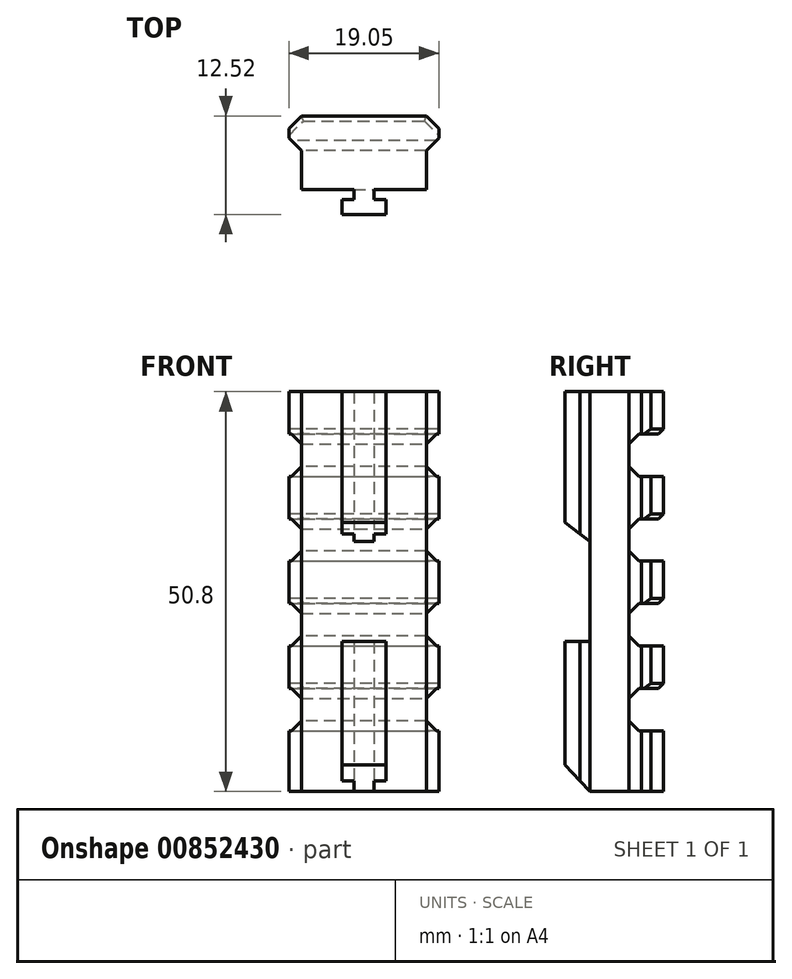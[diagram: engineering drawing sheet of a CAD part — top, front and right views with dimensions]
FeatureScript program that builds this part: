
annotation { "Feature Type Name" : "Feature", "Feature Type Description" : "" }
export const myFeature = defineFeature(function(context is Context, id is Id, definition is map)
    precondition{}
    {
        {
            var Q0;
            Q0=qCreatedBy(makeId("Top.planeOp"),FACE);
            var sketch = newSketch(context, id + "F0", { "sketchPlane" : qUnion([Q0])});
            skLineSegment(sketch, "E0.bottom", {"start": v(5.5, 6.04) * mm, "end": v(21.38, 6.04) * mm});
            skLineSegment(sketch, "E0.top", {"start": v(5.5, 11) * mm, "end": v(21.38, 11) * mm});
            skLineSegment(sketch, "E0.left", {"start": v(5.5, 6.04) * mm, "end": v(5.5, 11) * mm});
            skLineSegment(sketch, "E0.right", {"start": v(21.38, 6.04) * mm, "end": v(21.38, 11) * mm});
            skSolve(sketch);
        }
        {
            var Q0;
            Q0 = qSketchRegion(id + "F0", true);
            extrude(context, id + "F1", {"entities" : qUnion([Q0]), "depth" : 50.8 * mm, "offsetDistance" : 25.4 * mm});
        }
        {
            var Q0;
            Q0=makeQuery(id+"F1.opExtrude","CAP_FACE",FACE,{"disambiguationData":[OSD([sQuery(id+"F0.wireOp",EDGE,"E0.bottom"),sQuery(id+"F0.wireOp",EDGE,"E0.top"),sQuery(id+"F0.wireOp",EDGE,"E0.left"),sQuery(id+"F0.wireOp",EDGE,"E0.right")])],"isStart":false});
            var sketch = newSketch(context, id + "F2", { "sketchPlane" : qUnion([Q0])});
            skLineSegment(sketch, "E1", {"start": v(5.5, 11) * mm, "end": v(3.92, 12.58) * mm});
            skLineSegment(sketch, "E2", {"start": v(3.92, 12.58) * mm, "end": v(3.92, 13.8) * mm});
            skLineSegment(sketch, "E3", {"start": v(3.92, 13.8) * mm, "end": v(5.5, 15.39) * mm});
            skLineSegment(sketch, "E4", {"start": v(13.44, 12.67) * mm, "end": v(13.44, 17.63) * mm, "construction": true});
            skPoint(sketch, "E4.startSnap0", {"position": v(13.44, 11) * mm});
            skLineSegment(sketch, "E5.MirrorCS", {"start": v(22.97, 13.8) * mm, "end": v(21.38, 15.39) * mm});
            skLineSegment(sketch, "E6.MirrorCS", {"start": v(22.97, 12.58) * mm, "end": v(22.97, 13.8) * mm});
            skLineSegment(sketch, "E7.MirrorCS", {"start": v(21.38, 11) * mm, "end": v(22.97, 12.58) * mm});
            skLineSegment(sketch, "E8", {"start": v(5.5, 15.39) * mm, "end": v(21.38, 15.39) * mm});
            skSolve(sketch);
        }
        {
            var Q0;
            Q0 = qSketchRegion(id + "F2", true);
            var Q1;
            Q1=makeQuery(id+"F2.imprint","IMPRINT",FACE,{"disambiguationData":[TD([[makeQuery(id+"F2.imprint","IMPRINT",EDGE,{"derivedFrom":sQuery(id+"F2.wireOp",EDGE,"E1")}),-1.0]])]});
            extrude(context, id + "F3", {"entities" : qUnion([Q0, Q1]), "operationType" : NewBodyOperationType.ADD, "oppositeDirection" : true, "depth" : 50.8 * mm, "offsetDistance" : 25.4 * mm});
        }
        {
            var Q0;
            {var subQ0=sQuery(id+"F0.wireOp",EDGE,"E0.top");Q0=makeQuery(id+"F3.boolean.opBoolean","MERGE",FACE,{"derivedFrom":[makeQuery(id+"F1.opExtrude","CAP_FACE",FACE,{"disambiguationData":[OSD([sQuery(id+"F0.wireOp",EDGE,"E0.bottom"),subQ0,sQuery(id+"F0.wireOp",EDGE,"E0.left"),sQuery(id+"F0.wireOp",EDGE,"E0.right")])],"isStart":false}),makeQuery(id+"F3.opExtrude","CAP_FACE",FACE,{"disambiguationData":[OSD([subQ0,sQuery(id+"F2.wireOp",EDGE,"E1"),sQuery(id+"F2.wireOp",EDGE,"E2"),sQuery(id+"F2.wireOp",EDGE,"E3"),sQuery(id+"F2.wireOp",EDGE,"E5.MirrorCS"),sQuery(id+"F2.wireOp",EDGE,"E6.MirrorCS"),sQuery(id+"F2.wireOp",EDGE,"E7.MirrorCS"),sQuery(id+"F2.wireOp",EDGE,"E8")])],"isStart":true})]});}
            var sketch = newSketch(context, id + "F4", { "sketchPlane" : qUnion([Q0])});
            skLineSegment(sketch, "E9.bottom", {"start": v(16.24, 6.04) * mm, "end": v(10.65, 6.04) * mm});
            skLineSegment(sketch, "E9.top", {"start": v(16.24, 2.87) * mm, "end": v(10.65, 2.87) * mm});
            skLineSegment(sketch, "E9.left", {"start": v(16.24, 6.04) * mm, "end": v(16.24, 2.87) * mm});
            skLineSegment(sketch, "E9.right", {"start": v(10.65, 6.04) * mm, "end": v(10.65, 2.87) * mm});
            skSolve(sketch);
        }
        {
            var Q0;
            Q0 = qSketchRegion(id + "F4", true);
            var Q1;
            {var subQ0=sQuery(id+"F0.wireOp",EDGE,"E0.top");Q1=makeQuery(id+"F3.boolean.opBoolean","MERGE",FACE,{"derivedFrom":[makeQuery(id+"F1.opExtrude","CAP_FACE",FACE,{"disambiguationData":[OSD([sQuery(id+"F0.wireOp",EDGE,"E0.bottom"),subQ0,sQuery(id+"F0.wireOp",EDGE,"E0.left"),sQuery(id+"F0.wireOp",EDGE,"E0.right")])],"isStart":true}),makeQuery(id+"F3.opExtrude","CAP_FACE",FACE,{"disambiguationData":[OSD([subQ0,sQuery(id+"F2.wireOp",EDGE,"E1"),sQuery(id+"F2.wireOp",EDGE,"E2"),sQuery(id+"F2.wireOp",EDGE,"E3"),sQuery(id+"F2.wireOp",EDGE,"E5.MirrorCS"),sQuery(id+"F2.wireOp",EDGE,"E6.MirrorCS"),sQuery(id+"F2.wireOp",EDGE,"E7.MirrorCS"),sQuery(id+"F2.wireOp",EDGE,"E8")])],"isStart":false})]});}
            extrude(context, id + "F5", {"entities" : qUnion([Q0]), "operationType" : NewBodyOperationType.ADD, "endBound" : BoundingType.UP_TO_SURFACE, "oppositeDirection" : true, "depth" : 25.4 * mm, "endBoundEntityFace" : qUnion([Q1]), "offsetDistance" : 25.4 * mm});
        }
        {
            var Q0;
            Q0=makeQuery(id+"F5.opExtrude","SWEPT_FACE",FACE,{"disambiguationData":[OSD([sQuery(id+"F4.wireOp",EDGE,"E9.top")])]});
            var sketch = newSketch(context, id + "F6", { "sketchPlane" : qUnion([Q0])});
            skLineSegment(sketch, "E10.bottom", {"start": v(16.24, 19.05) * mm, "end": v(10.65, 19.05) * mm});
            skLineSegment(sketch, "E10.top", {"start": v(16.24, 31.75) * mm, "end": v(10.65, 31.75) * mm});
            skLineSegment(sketch, "E10.left", {"start": v(16.24, 19.05) * mm, "end": v(16.24, 31.75) * mm});
            skLineSegment(sketch, "E10.right", {"start": v(10.65, 19.05) * mm, "end": v(10.65, 31.75) * mm});
            skSolve(sketch);
        }
        {
            var Q0;
            Q0 = qSketchRegion(id + "F6", true);
            var Q1;
            {var subQ9=sQuery(id+"F0.wireOp",EDGE,"E0.left");var subQ10=sQuery(id+"F0.wireOp",EDGE,"E0.bottom");Q1=makeQuery(id+"F5.boolean.opBoolean","SPLIT",FACE,{"disambiguationData":[TD([makeQuery(id+"F1.opExtrude","SWEPT_FACE",FACE,{"disambiguationData":[OSD([subQ9])]})])],"derivedFrom":makeQuery(id+"F1.opExtrude","SWEPT_FACE",FACE,{"disambiguationData":[OSD([subQ10])]})});}
            extrude(context, id + "F7", {"entities" : qUnion([Q0]), "operationType" : NewBodyOperationType.REMOVE, "endBound" : BoundingType.UP_TO_SURFACE, "oppositeDirection" : true, "depth" : 25.4 * mm, "endBoundEntityFace" : qUnion([Q1]), "offsetDistance" : 25.4 * mm});
        }
        {
            var Q0;
            {var subQ0=sQuery(id+"F0.wireOp",EDGE,"E0.top");Q0=makeQuery(id+"F5.boolean.opBoolean","MERGE",FACE,{"derivedFrom":[makeQuery(id+"F3.boolean.opBoolean","MERGE",FACE,{"derivedFrom":[makeQuery(id+"F1.opExtrude","CAP_FACE",FACE,{"disambiguationData":[OSD([sQuery(id+"F0.wireOp",EDGE,"E0.bottom"),subQ0,sQuery(id+"F0.wireOp",EDGE,"E0.left"),sQuery(id+"F0.wireOp",EDGE,"E0.right")])],"isStart":true}),makeQuery(id+"F3.opExtrude","CAP_FACE",FACE,{"disambiguationData":[OSD([subQ0,sQuery(id+"F2.wireOp",EDGE,"E1"),sQuery(id+"F2.wireOp",EDGE,"E2"),sQuery(id+"F2.wireOp",EDGE,"E3"),sQuery(id+"F2.wireOp",EDGE,"E5.MirrorCS"),sQuery(id+"F2.wireOp",EDGE,"E6.MirrorCS"),sQuery(id+"F2.wireOp",EDGE,"E7.MirrorCS"),sQuery(id+"F2.wireOp",EDGE,"E8")])],"isStart":false})]}),makeQuery(id+"F5.opExtrude","CAP_FACE",FACE,{"disambiguationData":[OSD([sQuery(id+"F4.wireOp",EDGE,"E9.bottom"),sQuery(id+"F4.wireOp",EDGE,"E9.top"),sQuery(id+"F4.wireOp",EDGE,"E9.left"),sQuery(id+"F4.wireOp",EDGE,"E9.right")])],"isStart":false})]});}
            var sketch = newSketch(context, id + "F8", { "sketchPlane" : qUnion([Q0])});
            skLineSegment(sketch, "E11.bottom", {"start": v(16.24, -6.04) * mm, "end": v(14.71, -6.04) * mm});
            skLineSegment(sketch, "E11.top", {"start": v(16.24, -4.77) * mm, "end": v(14.71, -4.77) * mm});
            skLineSegment(sketch, "E11.left", {"start": v(16.24, -6.04) * mm, "end": v(16.24, -4.77) * mm});
            skLineSegment(sketch, "E11.right", {"start": v(14.71, -6.04) * mm, "end": v(14.71, -4.77) * mm});
            skLineSegment(sketch, "E12", {"start": v(13.44, -2.87) * mm, "end": v(13.44, -7.3) * mm, "construction": true});
            skLineSegment(sketch, "E13.MirrorCS", {"start": v(12.17, -6.04) * mm, "end": v(12.17, -4.77) * mm});
            skLineSegment(sketch, "E14.MirrorCS", {"start": v(10.65, -6.04) * mm, "end": v(12.17, -6.04) * mm});
            skLineSegment(sketch, "E15.MirrorCS", {"start": v(10.65, -4.77) * mm, "end": v(12.17, -4.77) * mm});
            skSolve(sketch);
        }
        {
            var Q0;
            Q0 = qSketchRegion(id + "F8", true);
            var Q1;
            Q1=makeQuery(id+"F8.imprint","IMPRINT",FACE,{"disambiguationData":[TD([[makeQuery(id+"F8.imprint","IMPRINT",EDGE,{"derivedFrom":sQuery(id+"F8.wireOp",EDGE,"E13.MirrorCS")}),1.0]])]});
            extrude(context, id + "F9", {"entities" : qUnion([Q0, Q1]), "operationType" : NewBodyOperationType.REMOVE, "endBound" : BoundingType.THROUGH_ALL, "oppositeDirection" : true, "depth" : 25.4 * mm, "offsetDistance" : 25.4 * mm});
        }
        {
            var Q0;
            {var subQ2=sQuery(id+"F4.wireOp",EDGE,"E9.left");var subQ4=sQuery(id+"F6.wireOp",EDGE,"E10.bottom");Q0=makeQuery(id+"F7.boolean.opBoolean","SPLIT",FACE,{"disambiguationData":[TD([makeQuery(id+"F7.opExtrude","SWEPT_FACE",FACE,{"disambiguationData":[OSD([subQ4])]})])],"derivedFrom":makeQuery(id+"F5.opExtrude","SWEPT_FACE",FACE,{"disambiguationData":[OSD([subQ2])]})});}
            var sketch = newSketch(context, id + "F10", { "sketchPlane" : qUnion([Q0])});
            skLineSegment(sketch, "E16", {"start": v(2.87, 3.4) * mm, "end": v(6.04, 0) * mm});
            skLineSegment(sketch, "E17", {"start": v(2.87, 34.2) * mm, "end": v(6.04, 31.75) * mm});
            skLineSegment(sketch, "E18", {"start": v(6.04, 0) * mm, "end": v(2.87, 0) * mm});
            skLineSegment(sketch, "E19", {"start": v(2.87, 0) * mm, "end": v(2.87, 3.4) * mm});
            skLineSegment(sketch, "E20", {"start": v(2.87, 34.2) * mm, "end": v(2.87, 31.75) * mm});
            skLineSegment(sketch, "E21", {"start": v(2.87, 31.75) * mm, "end": v(6.04, 31.75) * mm});
            skSolve(sketch);
        }
        {
            var Q0;
            Q0 = qSketchRegion(id + "F10", true);
            extrude(context, id + "F11", {"entities" : qUnion([Q0]), "operationType" : NewBodyOperationType.REMOVE, "endBound" : BoundingType.UP_TO_NEXT, "oppositeDirection" : true, "depth" : 25.4 * mm, "offsetDistance" : 25.4 * mm});
        }
        {
            var Q0;
            Q0=makeQuery(id+"F1.opExtrude","SWEPT_FACE",FACE,{"disambiguationData":[OSD([sQuery(id+"F0.wireOp",EDGE,"E0.right")])]});
            var sketch = newSketch(context, id + "F12", { "sketchPlane" : qUnion([Q0])});
            skLineSegment(sketch, "E22.bottom", {"start": v(11, 45.42) * mm, "end": v(15.39, 45.42) * mm});
            skLineSegment(sketch, "E22.top", {"start": v(11, 40.03) * mm, "end": v(15.39, 40.03) * mm});
            skLineSegment(sketch, "E22.left", {"start": v(11, 45.42) * mm, "end": v(11, 40.03) * mm});
            skLineSegment(sketch, "E22.right", {"start": v(15.39, 45.42) * mm, "end": v(15.39, 40.03) * mm});
            skLineSegment(sketch, "E23.bottom", {"start": v(11, 34.65) * mm, "end": v(15.39, 34.65) * mm});
            skLineSegment(sketch, "E23.top", {"start": v(11, 29.26) * mm, "end": v(15.39, 29.26) * mm});
            skLineSegment(sketch, "E23.left", {"start": v(11, 34.65) * mm, "end": v(11, 29.26) * mm});
            skLineSegment(sketch, "E23.right", {"start": v(15.39, 34.65) * mm, "end": v(15.39, 29.26) * mm});
            skLineSegment(sketch, "E24.bottom", {"start": v(11, 23.88) * mm, "end": v(15.39, 23.88) * mm});
            skLineSegment(sketch, "E24.top", {"start": v(11, 18.5) * mm, "end": v(15.39, 18.5) * mm});
            skLineSegment(sketch, "E24.left", {"start": v(11, 23.88) * mm, "end": v(11, 18.5) * mm});
            skLineSegment(sketch, "E24.right", {"start": v(15.39, 23.88) * mm, "end": v(15.39, 18.5) * mm});
            skLineSegment(sketch, "E25.bottom", {"start": v(11, 13.1) * mm, "end": v(15.39, 13.1) * mm});
            skLineSegment(sketch, "E25.top", {"start": v(11, 7.72) * mm, "end": v(15.39, 7.72) * mm});
            skLineSegment(sketch, "E25.left", {"start": v(11, 13.1) * mm, "end": v(11, 7.72) * mm});
            skLineSegment(sketch, "E25.right", {"start": v(15.39, 13.1) * mm, "end": v(15.39, 7.72) * mm});
            skSolve(sketch);
        }
        {
            var Q0;
            Q0 = qSketchRegion(id + "F12", true);
            extrude(context, id + "F13", {"entities" : qUnion([Q0]), "operationType" : NewBodyOperationType.REMOVE, "endBound" : BoundingType.SYMMETRIC, "oppositeDirection" : true, "depth" : 50.8 * mm, "offsetDistance" : 25.4 * mm});
        }
        {
            var Q0;
            Q0=makeQuery(id+"F13.boolean.opBoolean","COPY",EDGE,{"derivedFrom":makeQuery(id+"F13.opExtrude","SWEPT_EDGE",EDGE,{"disambiguationData":[OSD([sQuery(id+"F0.wireOp",EDGE,"E0.top"),sQuery(id+"F0.wireOp",EDGE,"E0.right"),sQuery(id+"F2.wireOp",EDGE,"E7.MirrorCS"),sQuery(id+"F12.wireOp",EDGE,"E25.top"),sQuery(id+"F12.wireOp",EDGE,"E25.left")])]})});
            var Q1;
            Q1=makeQuery(id+"F13.boolean.opBoolean","COPY",EDGE,{"derivedFrom":makeQuery(id+"F13.opExtrude","SWEPT_EDGE",EDGE,{"disambiguationData":[OSD([sQuery(id+"F0.wireOp",EDGE,"E0.top"),sQuery(id+"F0.wireOp",EDGE,"E0.right"),sQuery(id+"F2.wireOp",EDGE,"E7.MirrorCS"),sQuery(id+"F12.wireOp",EDGE,"E25.bottom"),sQuery(id+"F12.wireOp",EDGE,"E25.left")])]})});
            var Q2;
            Q2=makeQuery(id+"F13.boolean.opBoolean","COPY",EDGE,{"derivedFrom":makeQuery(id+"F13.opExtrude","SWEPT_EDGE",EDGE,{"disambiguationData":[OSD([sQuery(id+"F0.wireOp",EDGE,"E0.top"),sQuery(id+"F0.wireOp",EDGE,"E0.right"),sQuery(id+"F2.wireOp",EDGE,"E7.MirrorCS"),sQuery(id+"F12.wireOp",EDGE,"E24.top"),sQuery(id+"F12.wireOp",EDGE,"E24.left")])]})});
            var Q3;
            Q3=makeQuery(id+"F13.boolean.opBoolean","COPY",EDGE,{"derivedFrom":makeQuery(id+"F13.opExtrude","SWEPT_EDGE",EDGE,{"disambiguationData":[OSD([sQuery(id+"F0.wireOp",EDGE,"E0.top"),sQuery(id+"F0.wireOp",EDGE,"E0.right"),sQuery(id+"F2.wireOp",EDGE,"E7.MirrorCS"),sQuery(id+"F12.wireOp",EDGE,"E24.bottom"),sQuery(id+"F12.wireOp",EDGE,"E24.left")])]})});
            var Q4;
            Q4=makeQuery(id+"F13.boolean.opBoolean","COPY",EDGE,{"derivedFrom":makeQuery(id+"F13.opExtrude","SWEPT_EDGE",EDGE,{"disambiguationData":[OSD([sQuery(id+"F0.wireOp",EDGE,"E0.top"),sQuery(id+"F0.wireOp",EDGE,"E0.right"),sQuery(id+"F2.wireOp",EDGE,"E7.MirrorCS"),sQuery(id+"F12.wireOp",EDGE,"E23.top"),sQuery(id+"F12.wireOp",EDGE,"E23.left")])]})});
            var Q5;
            Q5=makeQuery(id+"F13.boolean.opBoolean","COPY",EDGE,{"derivedFrom":makeQuery(id+"F13.opExtrude","SWEPT_EDGE",EDGE,{"disambiguationData":[OSD([sQuery(id+"F0.wireOp",EDGE,"E0.top"),sQuery(id+"F0.wireOp",EDGE,"E0.right"),sQuery(id+"F2.wireOp",EDGE,"E7.MirrorCS"),sQuery(id+"F12.wireOp",EDGE,"E23.bottom"),sQuery(id+"F12.wireOp",EDGE,"E23.left")])]})});
            var Q6;
            Q6=makeQuery(id+"F13.boolean.opBoolean","COPY",EDGE,{"derivedFrom":makeQuery(id+"F13.opExtrude","SWEPT_EDGE",EDGE,{"disambiguationData":[OSD([sQuery(id+"F0.wireOp",EDGE,"E0.top"),sQuery(id+"F0.wireOp",EDGE,"E0.right"),sQuery(id+"F2.wireOp",EDGE,"E7.MirrorCS"),sQuery(id+"F12.wireOp",EDGE,"E22.top"),sQuery(id+"F12.wireOp",EDGE,"E22.left")])]})});
            var Q7;
            Q7=makeQuery(id+"F13.boolean.opBoolean","COPY",EDGE,{"derivedFrom":makeQuery(id+"F13.opExtrude","SWEPT_EDGE",EDGE,{"disambiguationData":[OSD([sQuery(id+"F0.wireOp",EDGE,"E0.top"),sQuery(id+"F0.wireOp",EDGE,"E0.right"),sQuery(id+"F2.wireOp",EDGE,"E7.MirrorCS"),sQuery(id+"F12.wireOp",EDGE,"E22.bottom"),sQuery(id+"F12.wireOp",EDGE,"E22.left")])]})});
            chamfer(context, id + "F14", {"entities" : qUnion([Q0, Q1, Q2, Q3, Q4, Q5, Q6, Q7]), "width" : 1.27 * mm, "tangentPropagation" : true});
        }
        {
            var Q0;
            Q0=makeQuery(id+"F13.boolean.opBoolean","COPY",EDGE,{"derivedFrom":makeQuery(id+"F13.opExtrude","SWEPT_EDGE",EDGE,{"disambiguationData":[OSD([sQuery(id+"F12.wireOp",EDGE,"E23.bottom"),sQuery(id+"F12.wireOp",EDGE,"E23.right")])]})});
            var Q1;
            Q1=makeQuery(id+"F13.boolean.opBoolean","COPY",EDGE,{"derivedFrom":makeQuery(id+"F13.opExtrude","SWEPT_EDGE",EDGE,{"disambiguationData":[OSD([sQuery(id+"F12.wireOp",EDGE,"E24.bottom"),sQuery(id+"F12.wireOp",EDGE,"E24.right")])]})});
            var Q2;
            Q2=makeQuery(id+"F13.boolean.opBoolean","COPY",EDGE,{"derivedFrom":makeQuery(id+"F13.opExtrude","SWEPT_EDGE",EDGE,{"disambiguationData":[OSD([sQuery(id+"F12.wireOp",EDGE,"E25.bottom"),sQuery(id+"F12.wireOp",EDGE,"E25.right")])]})});
            var Q3;
            Q3=makeQuery(id+"F13.boolean.opBoolean","COPY",EDGE,{"derivedFrom":makeQuery(id+"F13.opExtrude","SWEPT_EDGE",EDGE,{"disambiguationData":[OSD([sQuery(id+"F12.wireOp",EDGE,"E22.bottom"),sQuery(id+"F12.wireOp",EDGE,"E22.right")])]})});
            var Q4;
            Q4=makeQuery(id+"F13.boolean.opBoolean","INTERSECT",EDGE,{"derivedFrom":[makeQuery(id+"F3.opExtrude","SWEPT_FACE",FACE,{"disambiguationData":[OSD([sQuery(id+"F2.wireOp",EDGE,"E5.MirrorCS")])]}),makeQuery(id+"F13.opExtrude","SWEPT_FACE",FACE,{"disambiguationData":[OSD([sQuery(id+"F12.wireOp",EDGE,"E22.bottom")])]})]});
            var Q5;
            Q5=makeQuery(id+"F13.boolean.opBoolean","INTERSECT",EDGE,{"derivedFrom":[makeQuery(id+"F3.opExtrude","SWEPT_FACE",FACE,{"disambiguationData":[OSD([sQuery(id+"F2.wireOp",EDGE,"E5.MirrorCS")])]}),makeQuery(id+"F13.opExtrude","SWEPT_FACE",FACE,{"disambiguationData":[OSD([sQuery(id+"F12.wireOp",EDGE,"E23.bottom")])]})]});
            var Q6;
            Q6=makeQuery(id+"F13.boolean.opBoolean","INTERSECT",EDGE,{"derivedFrom":[makeQuery(id+"F3.opExtrude","SWEPT_FACE",FACE,{"disambiguationData":[OSD([sQuery(id+"F2.wireOp",EDGE,"E5.MirrorCS")])]}),makeQuery(id+"F13.opExtrude","SWEPT_FACE",FACE,{"disambiguationData":[OSD([sQuery(id+"F12.wireOp",EDGE,"E24.bottom")])]})]});
            var Q7;
            Q7=makeQuery(id+"F13.boolean.opBoolean","INTERSECT",EDGE,{"derivedFrom":[makeQuery(id+"F3.opExtrude","SWEPT_FACE",FACE,{"disambiguationData":[OSD([sQuery(id+"F2.wireOp",EDGE,"E5.MirrorCS")])]}),makeQuery(id+"F13.opExtrude","SWEPT_FACE",FACE,{"disambiguationData":[OSD([sQuery(id+"F12.wireOp",EDGE,"E25.bottom")])]})]});
            var Q8;
            Q8=makeQuery(id+"F13.boolean.opBoolean","INTERSECT",EDGE,{"derivedFrom":[makeQuery(id+"F3.opExtrude","SWEPT_FACE",FACE,{"disambiguationData":[OSD([sQuery(id+"F2.wireOp",EDGE,"E3")])]}),makeQuery(id+"F13.opExtrude","SWEPT_FACE",FACE,{"disambiguationData":[OSD([sQuery(id+"F12.wireOp",EDGE,"E25.bottom")])]})]});
            var Q9;
            Q9=makeQuery(id+"F13.boolean.opBoolean","INTERSECT",EDGE,{"derivedFrom":[makeQuery(id+"F3.opExtrude","SWEPT_FACE",FACE,{"disambiguationData":[OSD([sQuery(id+"F2.wireOp",EDGE,"E3")])]}),makeQuery(id+"F13.opExtrude","SWEPT_FACE",FACE,{"disambiguationData":[OSD([sQuery(id+"F12.wireOp",EDGE,"E24.bottom")])]})]});
            var Q10;
            Q10=makeQuery(id+"F13.boolean.opBoolean","INTERSECT",EDGE,{"derivedFrom":[makeQuery(id+"F3.opExtrude","SWEPT_FACE",FACE,{"disambiguationData":[OSD([sQuery(id+"F2.wireOp",EDGE,"E3")])]}),makeQuery(id+"F13.opExtrude","SWEPT_FACE",FACE,{"disambiguationData":[OSD([sQuery(id+"F12.wireOp",EDGE,"E23.bottom")])]})]});
            var Q11;
            Q11=makeQuery(id+"F13.boolean.opBoolean","INTERSECT",EDGE,{"derivedFrom":[makeQuery(id+"F3.opExtrude","SWEPT_FACE",FACE,{"disambiguationData":[OSD([sQuery(id+"F2.wireOp",EDGE,"E3")])]}),makeQuery(id+"F13.opExtrude","SWEPT_FACE",FACE,{"disambiguationData":[OSD([sQuery(id+"F12.wireOp",EDGE,"E22.bottom")])]})]});
            chamfer(context, id + "F15", {"entities" : qUnion([Q0, Q1, Q2, Q3, Q4, Q5, Q6, Q7, Q8, Q9, Q10, Q11]), "width" : 0.64 * mm, "tangentPropagation" : true});
        }
    });
